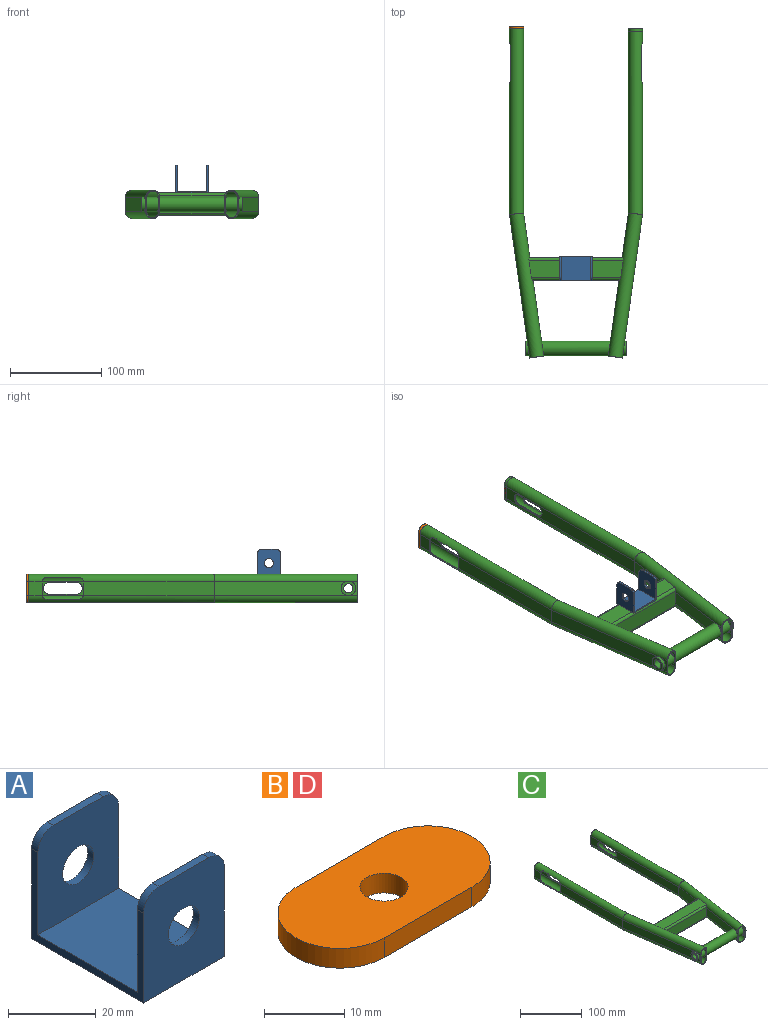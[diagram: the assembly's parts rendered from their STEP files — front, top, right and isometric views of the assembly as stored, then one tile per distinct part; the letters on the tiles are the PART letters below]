
ASSEMBLY  parts=4 mates=3
PART A: 16 faces, bbox 26x36x30 mm
  f0: plane 30x26mm, normal (0,1,0), area 690.7mm2, adj f1,f7,f8,f9,f11,f13,f15
  f1: plane 16x2mm, normal (0,0,1), area 32mm2, adj f0,f2,f13,f15
  f2: plane 28x26mm, normal (0,-1,0), area 638.7mm2, adj f1,f3,f8,f9,f11,f13,f15
  f3: plane 32x26mm, normal (0,0,1), area 832mm2, adj f2,f4,f8,f9
  f4: plane 28x26mm, normal (0,1,0), area 638.7mm2, adj f3,f5,f8,f9,f10,f12,f14
  f5: plane 16x2mm, normal (0,0,1), area 32mm2, adj f4,f6,f12,f14
  f6: plane 30x26mm, normal (0,-1,0), area 690.7mm2, adj f5,f7,f8,f9,f10,f12,f14
  f7: plane 36x26mm, normal (0,0,-1), area 936mm2, adj f0,f6,f8,f9
  f8: plane 36x25mm, normal (1,0,0), area 164mm2, adj f0,f2,f3,f4,f6,f7,f14,f15
  f9: plane 36x25mm, normal (-1,0,0), area 164mm2, adj f0,f2,f3,f4,f6,f7,f12,f13
  f10: cylinder r=5mm len=10mm, axis (0,-1,0), area 62.8mm2, adj f4,f6
  f11: cylinder r=5mm len=10mm, axis (0,-1,0), area 62.8mm2, adj f0,f2
  f12: cylinder r=5mm len=5mm, axis (0,-1,0), area 15.7mm2, adj f4,f5,f6,f9
  f13: cylinder r=5mm len=5mm, axis (0,-1,0), area 15.7mm2, adj f0,f1,f2,f9
  f14: cylinder r=5mm len=5mm, axis (0,1,0), area 15.7mm2, adj f4,f5,f6,f8
  f15: cylinder r=5mm len=5mm, axis (0,1,0), area 15.7mm2, adj f0,f1,f2,f8
PART B: 7 faces, bbox 31x15.5x3 mm
  f0: cylinder r=7.75mm len=15.5mm, axis (0,0,-1), area 73mm2, adj f1,f3,f5,f6
  f1: plane 15.5x3mm, normal (0,1,0), area 46.5mm2, adj f0,f2,f5,f6
  f2: cylinder r=7.75mm len=15.5mm, axis (0,0,-1), area 73mm2, adj f1,f3,f5,f6
  f3: plane 15.5x3mm, normal (0,-1,0), area 46.5mm2, adj f0,f2,f5,f6
  f4: cylinder r=3mm len=6mm, axis (0,0,-1), area 56.5mm2, adj f5,f6
  f5: plane 31x15.5mm, normal (0,0,1), area 400.7mm2, adj f0,f1,f2,f3,f4
  f6: plane 31x15.5mm, normal (0,0,-1), area 400.7mm2, adj f0,f1,f2,f3,f4
PART C: 104 faces, bbox 145.5x360x31 mm
  f0: plane 15.5x6.34mm, normal (0.99,0.14,0), area 29.4mm2, adj f1,f2,f18,f88
  f1: cylinder r=7.75mm len=159.19mm, axis (0.14,-0.99,0), area 3721.8mm2, adj f0,f7,f8,f12,f18,f20,f21,f38
  f2: cylinder r=7.75mm len=159.19mm, axis (0.14,-0.99,0), area 3721.8mm2, adj f0,f7,f8,f18,f20,f21,f23,f37
  f3: plane 15.5x8.33mm, normal (0.99,0.14,0), area 60.6mm2, adj f4,f6,f18,f47
  f4: cylinder r=6.55mm len=158.77mm, axis (0.14,-0.99,0), area 3250.5mm2, adj f3,f5,f13,f14,f16,f18,f47
  f5: plane 15.5x6.51mm, normal (-0.99,-0.14,0), area 32mm2, adj f4,f6,f18,f47
  f6: cylinder r=6.55mm len=158.77mm, axis (0.14,-0.99,0), area 3250.5mm2, adj f3,f5,f9,f13,f14,f18,f47
  f7: plane 15.5x8.5mm, normal (-0.99,-0.14,0), area 63.2mm2, adj f1,f2,f18,f46
  f8: plane 72.35x15.5mm, normal (0.99,0.14,0), area 1062.6mm2, adj f1,f2,f39,f88
  f9: cylinder r=6.55mm len=202.82mm, axis (0,-1,0), area 3967.5mm2, adj f6,f10,f15,f17,f19,f32,f33,f34
  f10: plane 15.5x14.82mm, normal (1,0,0), area 228.8mm2, adj f9,f16,f19,f30,f31,f32
  f11: plane 15.5x14.82mm, normal (-1,0,0), area 228.8mm2, adj f12,f19,f23,f30,f31,f32
  f12: cylinder r=7.75mm len=202.9mm, axis (0,-1,0), area 4735.5mm2, adj f1,f11,f19,f22,f24,f32,f33,f34
  f13: plane 144.65x20.33mm, normal (0.99,0.14,0), area 2194.3mm2, adj f4,f6,f17,f47
  f14: plane 145.56x20.46mm, normal (-0.99,-0.14,0), area 2208.6mm2, adj f4,f6,f15,f47
  f15: plane 201.9x15.5mm, normal (-1,0,0), area 2613.2mm2, adj f9,f14,f16,f19,f25,f26,f27,f28
  f16: cylinder r=6.55mm len=202.82mm, axis (0,-1,0), area 3967.5mm2, adj f4,f10,f15,f17,f19,f29,f30,f36
  f17: plane 143.08x15.5mm, normal (1,0,0), area 2217mm2, adj f9,f13,f16,f34,f35,f36
  f18: plane 31x15.35mm, normal (0.14,-0.99,0), area 91.1mm2, adj f0,f1,f2,f3,f4,f5,f6,f7
  f19: plane 31x15.5mm, normal (0,1,0), area 91.1mm2, adj f9,f10,f11,f12,f15,f16,f23,f24
  f20: plane 48.3x15.5mm, normal (0.99,0.14,0), area 756mm2, adj f1,f2,f24,f38
  f21: plane 144.56x20.32mm, normal (-0.99,-0.14,0), area 2193mm2, adj f1,f2,f22,f46
  f22: plane 143.17x15.5mm, normal (-1,0,0), area 2218.3mm2, adj f12,f21,f23,f34,f35,f36
  f23: cylinder r=7.75mm len=202.9mm, axis (0,-1,0), area 4735.5mm2, adj f2,f11,f19,f22,f24,f29,f30,f36
  f24: plane 201.82x15.5mm, normal (1,0,0), area 2611.9mm2, adj f12,f19,f20,f23,f25,f26,f27,f28
  f25: plane 29.5x1.2mm, normal (0,0,-1), area 35.4mm2, adj f15,f24,f26,f28
  f26: cylinder r=6.5mm len=13mm, axis (1,0,0), area 24.5mm2, adj f15,f24,f25,f27
  f27: plane 29.5x1.2mm, normal (0,0,1), area 35.4mm2, adj f15,f24,f26,f28
  f28: cylinder r=6.5mm len=13mm, axis (1,0,0), area 24.5mm2, adj f15,f24,f25,f27
  f29: plane 35.05x1.57mm, normal (0,0,-1), area 52.5mm2, adj f16,f23,f30,f36
  f30: cylinder r=5.03mm len=5.03mm, axis (-1,0,0), area 10.5mm2, adj f10,f11,f16,f23,f29,f31
  f31: plane 14x1.2mm, normal (0,-1,0), area 16.8mm2, adj f10,f11,f30,f32
  f32: cylinder r=5.03mm len=5.03mm, axis (-1,0,0), area 10.5mm2, adj f9,f10,f11,f12,f31,f33
  f33: plane 35.05x1.57mm, normal (0,0,1), area 52.5mm2, adj f9,f12,f32,f34
  f34: cylinder r=5mm len=5mm, axis (-1,0,0), area 10.4mm2, adj f9,f12,f17,f22,f33,f35
  f35: plane 14x1.2mm, normal (0,1,0), area 16.8mm2, adj f17,f22,f34,f36
  f36: cylinder r=5mm len=5mm, axis (-1,0,0), area 10.4mm2, adj f16,f17,f22,f23,f29,f35
  f37: plane 103.36x19mm, normal (0,0,1), area 1913.2mm2, adj f2,f41,f42,f80
  f38: plane 101.34x19.01mm, normal (0,1,0), area 1918mm2, adj f1,f2,f20,f41,f43,f67,f80,f83
  f39: plane 94.31x19.01mm, normal (0,-1,0), area 1784.5mm2, adj f1,f2,f8,f42,f44,f80,f82,f83
  f40: plane 103.36x19mm, normal (0,0,-1), area 1913.2mm2, adj f1,f43,f44,f83
  f41: cylinder r=3mm len=103.44mm, axis (-1,0,0), area 483.6mm2, adj f2,f37,f38,f80
  f42: cylinder r=3mm len=98.02mm, axis (1,0,0), area 453.4mm2, adj f2,f37,f39,f80
  f43: cylinder r=3mm len=103.44mm, axis (1,0,0), area 483.6mm2, adj f1,f38,f40,f83
  f44: cylinder r=3mm len=98.02mm, axis (-1,0,0), area 453.4mm2, adj f1,f39,f40,f83
  f45: plane 16x16mm, normal (-1,0,0), area 122.5mm2, adj f46,f89
  f46: cylinder r=8mm len=16mm, axis (-1,0,0), area 143.1mm2, adj f1,f2,f7,f21,f45
  f47: cylinder r=8mm len=16mm, axis (-1,0,0), area 664.9mm2, adj f3,f4,f5,f6,f13,f14
  f48: cylinder r=8mm len=16mm, axis (-1,0,0), area 664.9mm2, adj f73,f74,f84,f85,f86,f87
  f49: cylinder r=8mm len=16mm, axis (-1,0,0), area 143.1mm2, adj f50,f66,f79,f80,f83
  f50: plane 16x16mm, normal (1,0,0), area 122.5mm2, adj f49,f89
  f51: cylinder r=5mm len=5mm, axis (1,0,0), area 10.4mm2, adj f52,f58,f64,f65,f70,f71
  f52: plane 14x1.2mm, normal (0,1,0), area 16.8mm2, adj f51,f53,f65,f70
  f53: cylinder r=5mm len=5mm, axis (1,0,0), area 10.4mm2, adj f52,f54,f65,f70,f75,f78
  f54: plane 35.05x1.57mm, normal (0,0,1), area 52.5mm2, adj f53,f55,f75,f78
  f55: cylinder r=5.03mm len=5.03mm, axis (1,0,0), area 10.5mm2, adj f54,f56,f75,f76,f77,f78
  f56: plane 14x1.2mm, normal (0,-1,0), area 16.8mm2, adj f55,f57,f76,f77
  f57: cylinder r=5.03mm len=5.03mm, axis (1,0,0), area 10.5mm2, adj f56,f58,f64,f71,f76,f77
  f58: plane 35.05x1.57mm, normal (0,0,-1), area 52.5mm2, adj f51,f57,f64,f71
  f59: cylinder r=6.5mm len=13mm, axis (-1,0,0), area 24.5mm2, adj f60,f62,f63,f72
  f60: plane 29.5x1.2mm, normal (0,0,1), area 35.4mm2, adj f59,f61,f63,f72
  f61: cylinder r=6.5mm len=13mm, axis (-1,0,0), area 24.5mm2, adj f60,f62,f63,f72
  f62: plane 29.5x1.2mm, normal (0,0,-1), area 35.4mm2, adj f59,f61,f63,f72
  f63: plane 201.82x15.5mm, normal (-1,0,0), area 2611.9mm2, adj f59,f60,f61,f62,f64,f67,f68,f75
  f64: cylinder r=7.75mm len=202.9mm, axis (0,-1,0), area 4735.5mm2, adj f51,f57,f58,f63,f65,f68,f76,f80
  f65: plane 143.17x15.5mm, normal (1,0,0), area 2218.3mm2, adj f51,f52,f53,f64,f75,f79
  f66: plane 15.5x8.5mm, normal (0.99,-0.14,0), area 63.2mm2, adj f49,f69,f80,f83
  f67: plane 48.3x15.5mm, normal (-0.99,0.14,0), area 756mm2, adj f38,f63,f80,f83
  f68: plane 31x15.5mm, normal (0,1,0), area 91.1mm2, adj f63,f64,f71,f72,f75,f76,f77,f78
  f69: plane 31x15.35mm, normal (-0.14,-0.99,0), area 91.1mm2, adj f66,f73,f74,f80,f81,f83,f84,f86
  f70: plane 143.08x15.5mm, normal (-1,0,0), area 2217mm2, adj f51,f52,f53,f71,f78,f87
  f71: cylinder r=6.55mm len=202.82mm, axis (0,-1,0), area 3967.5mm2, adj f51,f57,f58,f68,f70,f72,f77,f86
  f72: plane 201.9x15.5mm, normal (1,0,0), area 2613.2mm2, adj f59,f60,f61,f62,f68,f71,f78,f85
  f73: plane 15.5x6.51mm, normal (0.99,-0.14,0), area 32mm2, adj f48,f69,f84,f86
  f74: plane 15.5x8.33mm, normal (-0.99,0.14,0), area 60.6mm2, adj f48,f69,f84,f86
  f75: cylinder r=7.75mm len=202.9mm, axis (0,-1,0), area 4735.5mm2, adj f53,f54,f55,f63,f65,f68,f76,f83
  f76: plane 15.5x14.82mm, normal (1,0,0), area 228.8mm2, adj f55,f56,f57,f64,f68,f75
  f77: plane 15.5x14.82mm, normal (-1,0,0), area 228.8mm2, adj f55,f56,f57,f68,f71,f78
  f78: cylinder r=6.55mm len=202.82mm, axis (0,-1,0), area 3967.5mm2, adj f53,f54,f55,f68,f70,f72,f77,f84
  f79: plane 144.56x20.32mm, normal (0.99,-0.14,0), area 2193mm2, adj f49,f65,f80,f83
  f80: cylinder r=7.75mm len=159.19mm, axis (-0.14,-0.99,0), area 3721.8mm2, adj f37,f38,f39,f41,f42,f49,f64,f66
  f81: plane 15.5x6.34mm, normal (-0.99,0.14,0), area 29.4mm2, adj f69,f80,f83,f88
  f82: plane 72.35x15.5mm, normal (-0.99,0.14,0), area 1062.6mm2, adj f39,f80,f83,f88
  f83: cylinder r=7.75mm len=159.19mm, axis (-0.14,-0.99,0), area 3721.8mm2, adj f38,f39,f40,f43,f44,f49,f66,f67
  f84: cylinder r=6.55mm len=158.77mm, axis (-0.14,-0.99,0), area 3250.5mm2, adj f48,f69,f73,f74,f78,f85,f87
  f85: plane 145.56x20.46mm, normal (0.99,-0.14,0), area 2208.6mm2, adj f48,f72,f84,f86
  f86: cylinder r=6.55mm len=158.77mm, axis (-0.14,-0.99,0), area 3250.5mm2, adj f48,f69,f71,f73,f74,f85,f87
  f87: plane 144.65x20.33mm, normal (-0.99,0.14,0), area 2194.3mm2, adj f48,f70,f84,f86
  f88: cylinder r=8mm len=75.26mm, axis (-1,0,0), area 3669.5mm2, adj f0,f1,f2,f8,f80,f81,f82,f83
  f89: cylinder r=5mm len=110mm, axis (1,0,0), area 3455.8mm2, adj f45,f50
  f90: cylinder r=7.75mm len=21.92mm, axis (-0.14,-0.99,0), area 70.5mm2, adj f92,f96,f97,f101,f102,f103
  f91: cylinder r=7.75mm len=21.92mm, axis (-0.14,-0.99,0), area 70.5mm2, adj f92,f97,f98,f99,f100,f101
  f92: plane 21.8x15.5mm, normal (-0.99,0.14,0), area 341.2mm2, adj f90,f91,f97,f101
  f93: plane 21.8x15.5mm, normal (0.99,0.14,0), area 341.2mm2, adj f94,f95,f97,f101
  f94: cylinder r=7.75mm len=21.92mm, axis (0.14,-0.99,0), area 70.5mm2, adj f93,f97,f98,f99,f100,f101
  f95: cylinder r=7.75mm len=21.92mm, axis (0.14,-0.99,0), area 70.5mm2, adj f93,f96,f97,f101,f102,f103
  f96: cylinder r=1.4mm len=96.09mm, axis (-1,0,0), area 209.8mm2, adj f90,f95,f97,f103
  f97: plane 94.76x19.01mm, normal (0,1,0), area 1793mm2, adj f90,f91,f92,f93,f94,f95,f96,f98
  f98: cylinder r=1.4mm len=96.09mm, axis (1,0,0), area 209.8mm2, adj f91,f94,f97,f99
  f99: plane 101.43x19mm, normal (0,0,1), area 1876.5mm2, adj f91,f94,f98,f100
  f100: cylinder r=1.4mm len=101.49mm, axis (-1,0,0), area 222.8mm2, adj f91,f94,f99,f101
  f101: plane 100.89x19.01mm, normal (0,-1,0), area 1909.5mm2, adj f90,f91,f92,f93,f94,f95,f100,f102
  f102: cylinder r=1.4mm len=101.49mm, axis (1,0,0), area 222.8mm2, adj f90,f95,f101,f103
  f103: plane 101.43x19mm, normal (0,0,-1), area 1876.5mm2, adj f90,f95,f96,f102
PART D: same geometry as B
PLACE A rot(axis=(0,0,1),90deg) t=(171.71,-96.09,126.96)mm
PLACE B rot(axis=(0.58,-0.58,0.58),120deg) t=(106.71,169.44,99.46)mm
PLACE C t=(171.71,166.44,99.46)mm fixed
PLACE D rot(axis=(-0.58,-0.58,-0.58),120deg) t=(236.71,163.44,99.46)mm
MATE fastened A.f7 <-> C.f37  axis (0,0,-1) through (171.71,-96.09,111.96)mm
MATE fastened D.f0 <-> C.f64  axis (0,1,0) through (236.71,166.44,107.21)mm
MATE fastened B.f0 <-> C.f16  axis (0,-1,0) through (106.71,166.44,107.21)mm
